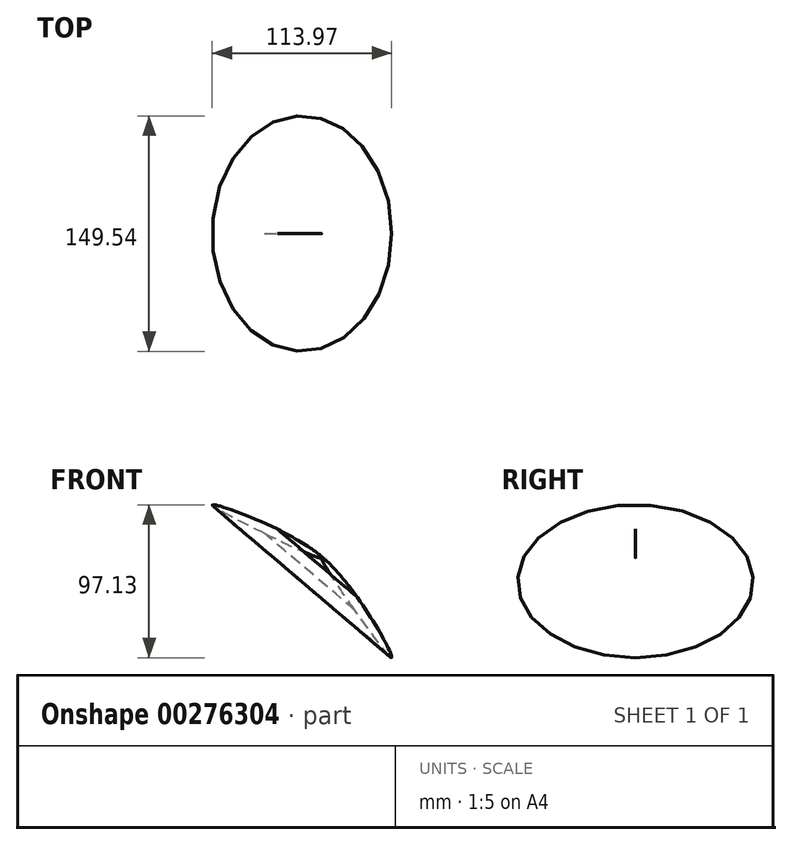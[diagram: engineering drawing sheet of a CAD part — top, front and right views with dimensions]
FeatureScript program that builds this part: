
annotation { "Feature Type Name" : "Feature", "Feature Type Description" : "" }
export const myFeature = defineFeature(function(context is Context, id is Id, definition is map)
    precondition{}
    {
        {
            var Q0;
            Q0=qCreatedBy(makeId("Front.planeOp"),FACE);
            var sketch = newSketch(context, id + "F0", { "sketchPlane" : qUnion([Q0])});
            skFitSpline(sketch, "E0", {"points": [v(0, 0) * mm, v(-41.22, 15.36) * mm, v(-13.74, 0) * mm, v(28.29, -18.39) * mm, v(0, 0) * mm]});
            skLineSegment(sketch, "E1", {"start": v(0, 0) * mm, "end": v(-7.98, -2.83) * mm});
            skLineSegment(sketch, "E2", {"start": v(28.29, -18.39) * mm, "end": v(34.95, -10.5) * mm});
            skLineSegment(sketch, "E3", {"start": v(34.95, -10.5) * mm, "end": v(22.22, -25.46) * mm});
            skSolve(sketch);
        }
        {
            var Q0;
            {var subQ0=sQuery(id+"F0.wireOp",EDGE,"E1");Q0=makeQuery(id+"F0.imprint","IMPRINT",FACE,{"disambiguationData":[TD([[makeQuery(id+"F0.imprint","IMPRINT",EDGE,{"derivedFrom":subQ0}),1.0]])]});}
            var Q1;
            {var subQ0=sQuery(id+"F0.wireOp",EDGE,"E1");Q1=makeQuery(id+"F0.imprint","IMPRINT",FACE,{"disambiguationData":[TD([[makeQuery(id+"F0.imprint","IMPRINT",EDGE,{"derivedFrom":subQ0}),-1.0]])]});}
            var Q2;
            Q2=sQuery(id+"F0.wireOp",EDGE,"E3");
            revolve(context, id + "F1", {"entities" : qUnion([Q0, Q1]), "axis" : qUnion([Q2]), "revolveType" : RevolveType.FULL});
        }
    });
